# Revit family: Profilschiene
name_source: partatom
category: Generic Models
revit_build: Autodesk Revit 2015 (Build: 20140606_1530(x64)
units: mm (PartAtom-declared; Revit-internal decimal feet)

## types (2) — shared parameters
Height = 12 mm  [stored 0.0393701 ft]
Height 1 = 2 mm  [stored 0.00656168 ft]
Length = 2000 mm  [stored 6.56168 ft]
Manufacturer = OBO Bettermann
Radius = 1 mm  [stored 0.00328084 ft]
URL = http://www.obo-bettermann.com
Width = 25 mm  [stored 0.082021 ft]
Width 1 = 6 mm  [stored 0.019685 ft]
Width/2 = 13 mm

## per-type parameters (varying)
| type | Article Type | GTIN | Manufacturer Art.No. | Material |
| 2066 2M FT | CL2512UP2000FT | 4012195046516 | 1117025 | OBO Hot - dip galvanized |
| 2066 2M FS | CL2512UP2000FS | 4012195046578 | 1117033 | Steel, Galvanized |

note: [stored X ft] marks values corroborated as IEEE doubles in the binary element streams (Revit-internal decimal feet)

## geometry (parser evidence)
native form markers: Sweep x2
no freeform markers — native parametric forms only
